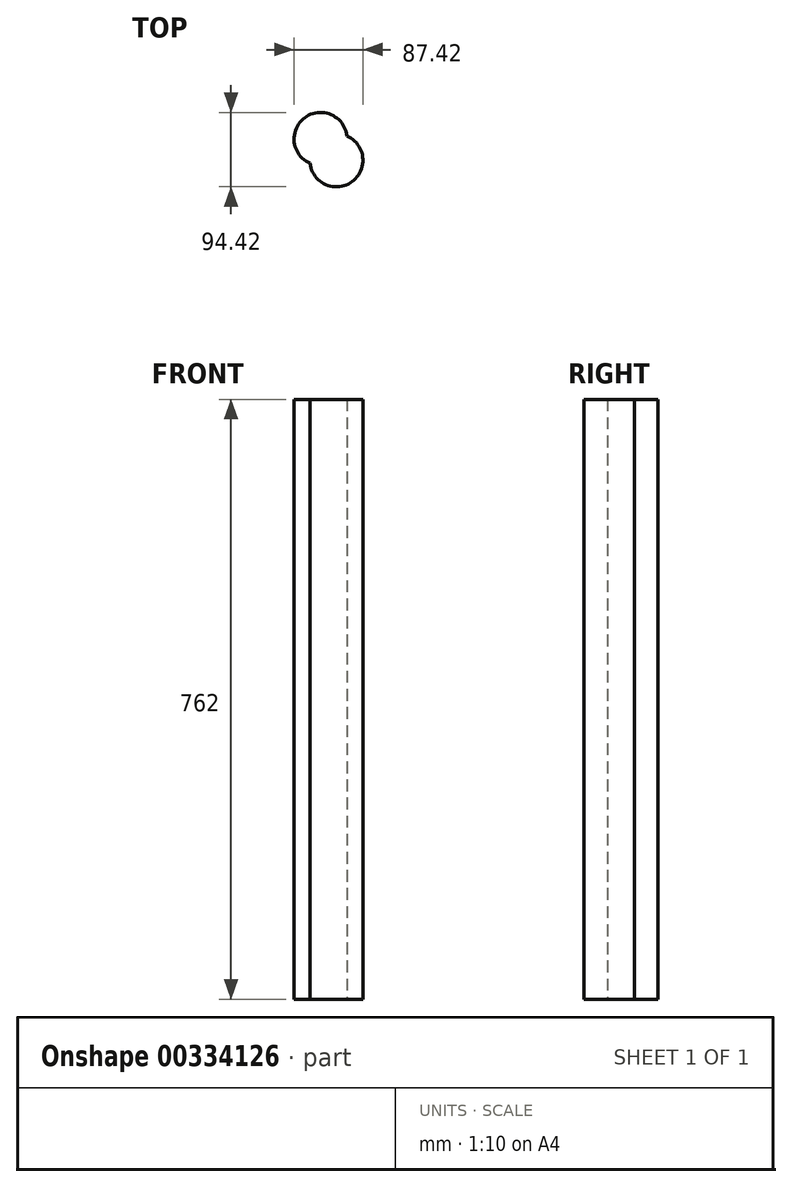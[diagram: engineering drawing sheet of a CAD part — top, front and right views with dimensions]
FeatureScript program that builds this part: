
annotation { "Feature Type Name" : "Feature", "Feature Type Description" : "" }
export const myFeature = defineFeature(function(context is Context, id is Id, definition is map)
    precondition{}
    {
        {
            var Q0;
            Q0=qCreatedBy(makeId("Top.planeOp"),FACE);
            var sketch = newSketch(context, id + "F0", { "sketchPlane" : qUnion([Q0])});
            skCircle(sketch, "E0", {"center": v(0, 0) * mm, "radius": 33.68 * mm});
            skCircle(sketch, "E1", {"center": v(20.06, -27.06) * mm, "radius": 33.68 * mm});
            skSolve(sketch);
        }
        {
            var Q0;
            Q0 = qSketchRegion(id + "F0", true);
            extrude(context, id + "F1", {"entities" : qUnion([Q0]), "depth" : 762 * mm});
        }
    });
